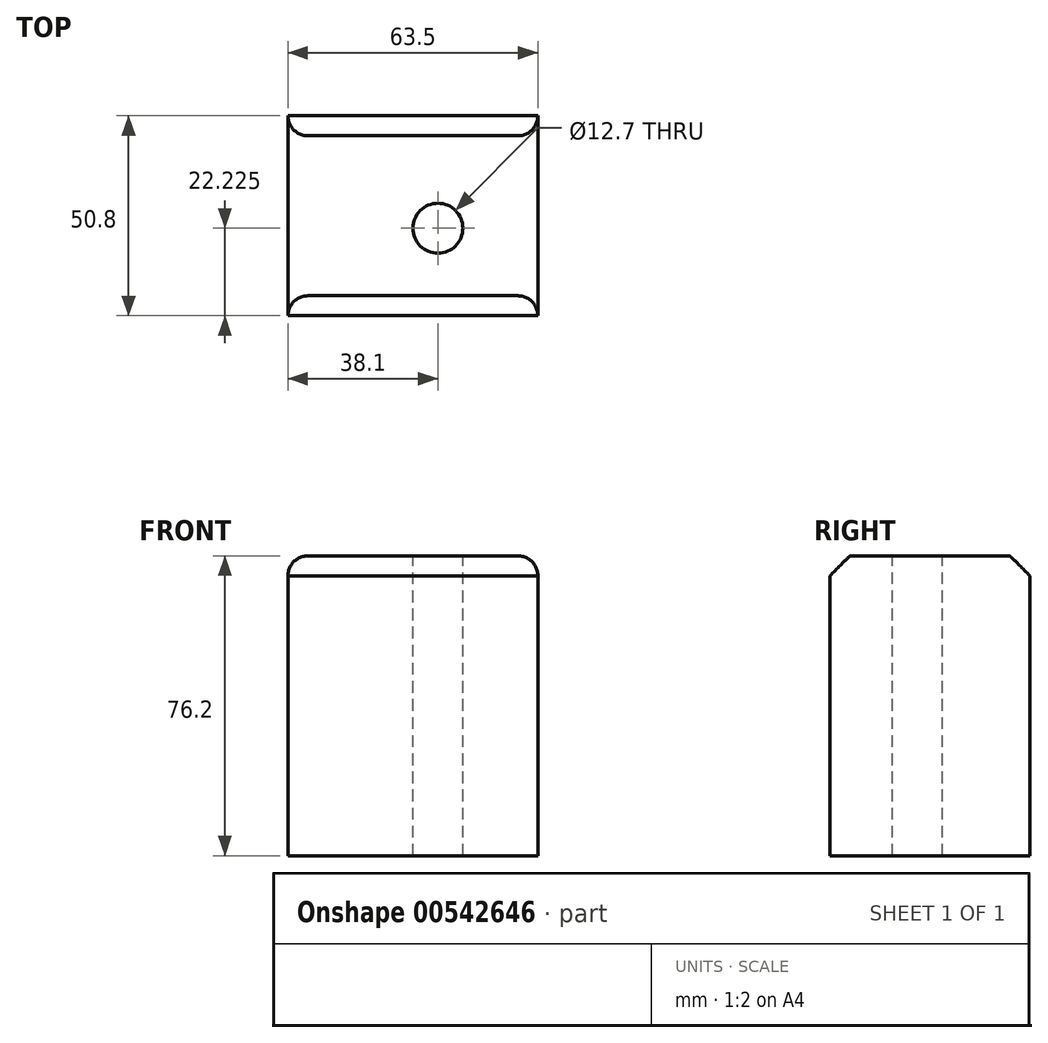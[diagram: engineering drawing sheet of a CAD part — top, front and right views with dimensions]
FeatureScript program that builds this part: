
annotation { "Feature Type Name" : "Feature", "Feature Type Description" : "" }
export const myFeature = defineFeature(function(context is Context, id is Id, definition is map)
    precondition{}
    {
        {
            var Q0;
            Q0=qCreatedBy(makeId("Top.planeOp"),FACE);
            var sketch = newSketch(context, id + "F0", { "sketchPlane" : qUnion([Q0])});
            skLineSegment(sketch, "E0.bottom", {"start": v(-25.4, 19.05) * mm, "end": v(38.1, 19.05) * mm});
            skLineSegment(sketch, "E0.top", {"start": v(-25.4, -31.75) * mm, "end": v(38.1, -31.75) * mm});
            skLineSegment(sketch, "E0.left", {"start": v(-25.4, 19.05) * mm, "end": v(-25.4, -31.75) * mm});
            skLineSegment(sketch, "E0.right", {"start": v(38.1, 19.05) * mm, "end": v(38.1, -31.75) * mm});
            skSolve(sketch);
        }
        {
            var Q0;
            Q0 = qSketchRegion(id + "F0", true);
            extrude(context, id + "F1", {"entities" : qUnion([Q0]), "depth" : 76.2 * mm, "offsetDistance" : 25.4 * mm});
        }
        {
            var Q0;
            Q0=makeQuery(id+"F1.opExtrude","CAP_FACE",FACE,{"disambiguationData":[OSD([sQuery(id+"F0.wireOp",EDGE,"E0.bottom"),sQuery(id+"F0.wireOp",EDGE,"E0.top"),sQuery(id+"F0.wireOp",EDGE,"E0.left"),sQuery(id+"F0.wireOp",EDGE,"E0.right")])],"isStart":false});
            var sketch = newSketch(context, id + "F2", { "sketchPlane" : qUnion([Q0])});
            skCircle(sketch, "E1", {"center": v(12.7, -9.53) * mm, "radius": 6.35 * mm});
            skSolve(sketch);
        }
        {
            var Q0;
            Q0 = qSketchRegion(id + "F2", true);
            extrude(context, id + "F3", {"entities" : qUnion([Q0]), "operationType" : NewBodyOperationType.REMOVE, "endBound" : BoundingType.THROUGH_ALL, "oppositeDirection" : true, "depth" : 25.4 * mm, "offsetDistance" : 25.4 * mm});
        }
        {
            var Q0;
            Q0=makeQuery(id+"F1.opExtrude","CAP_EDGE",EDGE,{"disambiguationData":[OSD([sQuery(id+"F0.wireOp",EDGE,"E0.bottom")])],"isStart":false});
            var Q1;
            Q1=makeQuery(id+"F1.opExtrude","CAP_EDGE",EDGE,{"disambiguationData":[OSD([sQuery(id+"F0.wireOp",EDGE,"E0.top")])],"isStart":false});
            chamfer(context, id + "F4", {"entities" : qUnion([Q0, Q1]), "width" : 5.08 * mm, "tangentPropagation" : true});
        }
        {
            var Q0;
            Q0=makeQuery(id+"F1.opExtrude","CAP_EDGE",EDGE,{"disambiguationData":[OSD([sQuery(id+"F0.wireOp",EDGE,"E0.left")])],"isStart":false});
            var Q1;
            Q1=makeQuery(id+"F1.opExtrude","CAP_EDGE",EDGE,{"disambiguationData":[OSD([sQuery(id+"F0.wireOp",EDGE,"E0.right")])],"isStart":false});
            fillet(context, id + "F5", {"entities" : qUnion([Q0, Q1]), "radius" : 5.08 * mm, "tangentPropagation" : true, "allowEdgeOverflow" : false});
        }
    });
